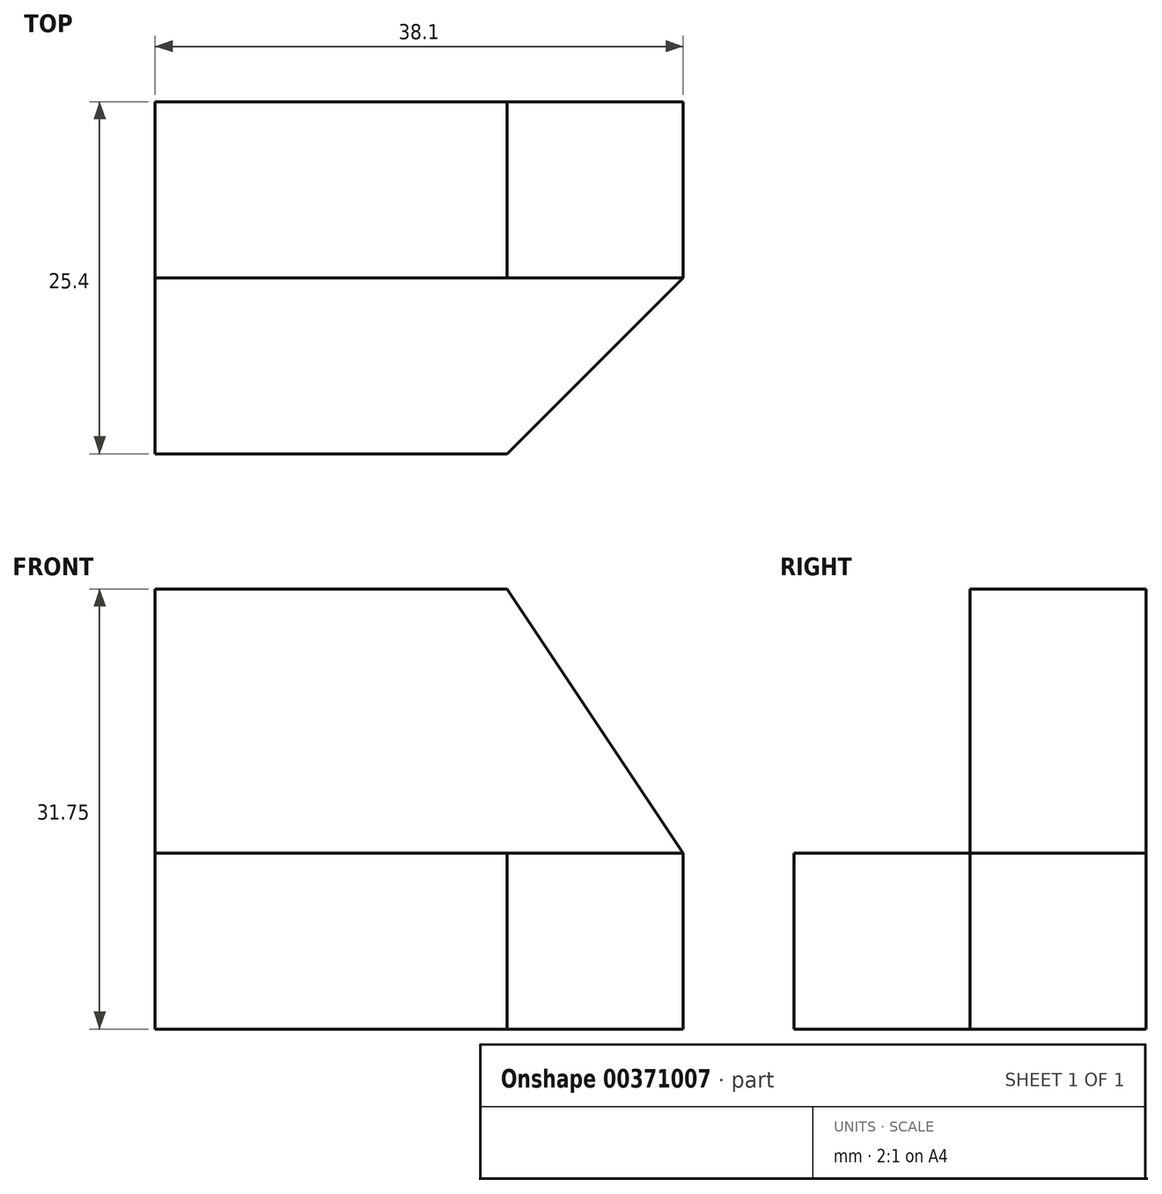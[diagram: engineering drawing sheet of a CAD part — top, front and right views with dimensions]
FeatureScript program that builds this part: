
annotation { "Feature Type Name" : "Feature", "Feature Type Description" : "" }
export const myFeature = defineFeature(function(context is Context, id is Id, definition is map)
    precondition{}
    {
        {
            var Q0;
            Q0=qCreatedBy(makeId("Front.planeOp"),FACE);
            var sketch = newSketch(context, id + "F0", { "sketchPlane" : qUnion([Q0])});
            skLineSegment(sketch, "E0", {"start": v(-21, 31.75) * mm, "end": v(-21, 0) * mm});
            skLineSegment(sketch, "E1", {"start": v(-21, 0) * mm, "end": v(17.1, 0) * mm});
            skLineSegment(sketch, "E2", {"start": v(-21, 31.75) * mm, "end": v(17.1, 31.75) * mm});
            skLineSegment(sketch, "E3", {"start": v(17.1, 31.75) * mm, "end": v(17.1, 0) * mm});
            skSolve(sketch);
        }
        {
            var Q0;
            Q0 = qSketchRegion(id + "F0", true);
            extrude(context, id + "F1", {"entities" : qUnion([Q0]), "depth" : 25.4 * mm});
        }
        {
            var Q0;
            Q0=makeQuery(id+"F1.opExtrude","CAP_FACE",FACE,{"disambiguationData":[OSD([sQuery(id+"F0.wireOp",EDGE,"E0"),sQuery(id+"F0.wireOp",EDGE,"E1"),sQuery(id+"F0.wireOp",EDGE,"E2"),sQuery(id+"F0.wireOp",EDGE,"E3")])],"isStart":false});
            var sketch = newSketch(context, id + "F2", { "sketchPlane" : qUnion([Q0])});
            skLineSegment(sketch, "E4", {"start": v(-21, 12.7) * mm, "end": v(17.1, 12.7) * mm});
            skSolve(sketch);
        }
        {
            var Q0;
            {var subQ0=sQuery(id+"F2.wireOp",EDGE,"E4");Q0=makeQuery(id+"F2.imprint","IMPRINT",FACE,{"disambiguationData":[TD([[makeQuery(id+"F2.imprint","IMPRINT",EDGE,{"derivedFrom":subQ0}),1.0]])]});}
            extrude(context, id + "F3", {"entities" : qUnion([Q0]), "operationType" : NewBodyOperationType.REMOVE, "oppositeDirection" : true, "depth" : 12.7 * mm});
        }
        {
            var Q0;
            Q0=makeQuery(id+"F3.boolean.opBoolean","COPY",FACE,{"derivedFrom":makeQuery(id+"F3.opExtrude","CAP_FACE",FACE,{"disambiguationData":[OSD([sQuery(id+"F0.wireOp",EDGE,"E0"),sQuery(id+"F0.wireOp",EDGE,"E2"),sQuery(id+"F0.wireOp",EDGE,"E3"),sQuery(id+"F2.wireOp",EDGE,"E4")])],"isStart":false})});
            var sketch = newSketch(context, id + "F4", { "sketchPlane" : qUnion([Q0])});
            skLineSegment(sketch, "E5", {"start": v(17.1, 12.7) * mm, "end": v(4.4, 31.75) * mm});
            skSolve(sketch);
        }
        {
            var Q0;
            {var subQ0=sQuery(id+"F4.wireOp",EDGE,"E5");Q0=makeQuery(id+"F4.imprint","IMPRINT",FACE,{"disambiguationData":[TD([[makeQuery(id+"F4.imprint","IMPRINT",EDGE,{"derivedFrom":subQ0}),-1.0]])]});}
            extrude(context, id + "F5", {"entities" : qUnion([Q0]), "operationType" : NewBodyOperationType.REMOVE, "oppositeDirection" : true, "depth" : 12.7 * mm});
        }
        {
            var Q0;
            Q0=makeQuery(id+"F3.boolean.opBoolean","COPY",FACE,{"derivedFrom":makeQuery(id+"F3.opExtrude","SWEPT_FACE",FACE,{"disambiguationData":[OSD([sQuery(id+"F2.wireOp",EDGE,"E4")])]})});
            var sketch = newSketch(context, id + "F6", { "sketchPlane" : qUnion([Q0])});
            skLineSegment(sketch, "E6", {"start": v(17.1, -12.7) * mm, "end": v(4.4, -25.4) * mm});
            skSolve(sketch);
        }
        {
            var Q0;
            {var subQ0=sQuery(id+"F6.wireOp",EDGE,"E6");Q0=makeQuery(id+"F6.imprint","IMPRINT",FACE,{"disambiguationData":[TD([[makeQuery(id+"F6.imprint","IMPRINT",EDGE,{"derivedFrom":subQ0}),1.0]])]});}
            extrude(context, id + "F7", {"entities" : qUnion([Q0]), "operationType" : NewBodyOperationType.REMOVE, "oppositeDirection" : true, "depth" : 12.7 * mm});
        }
    });
